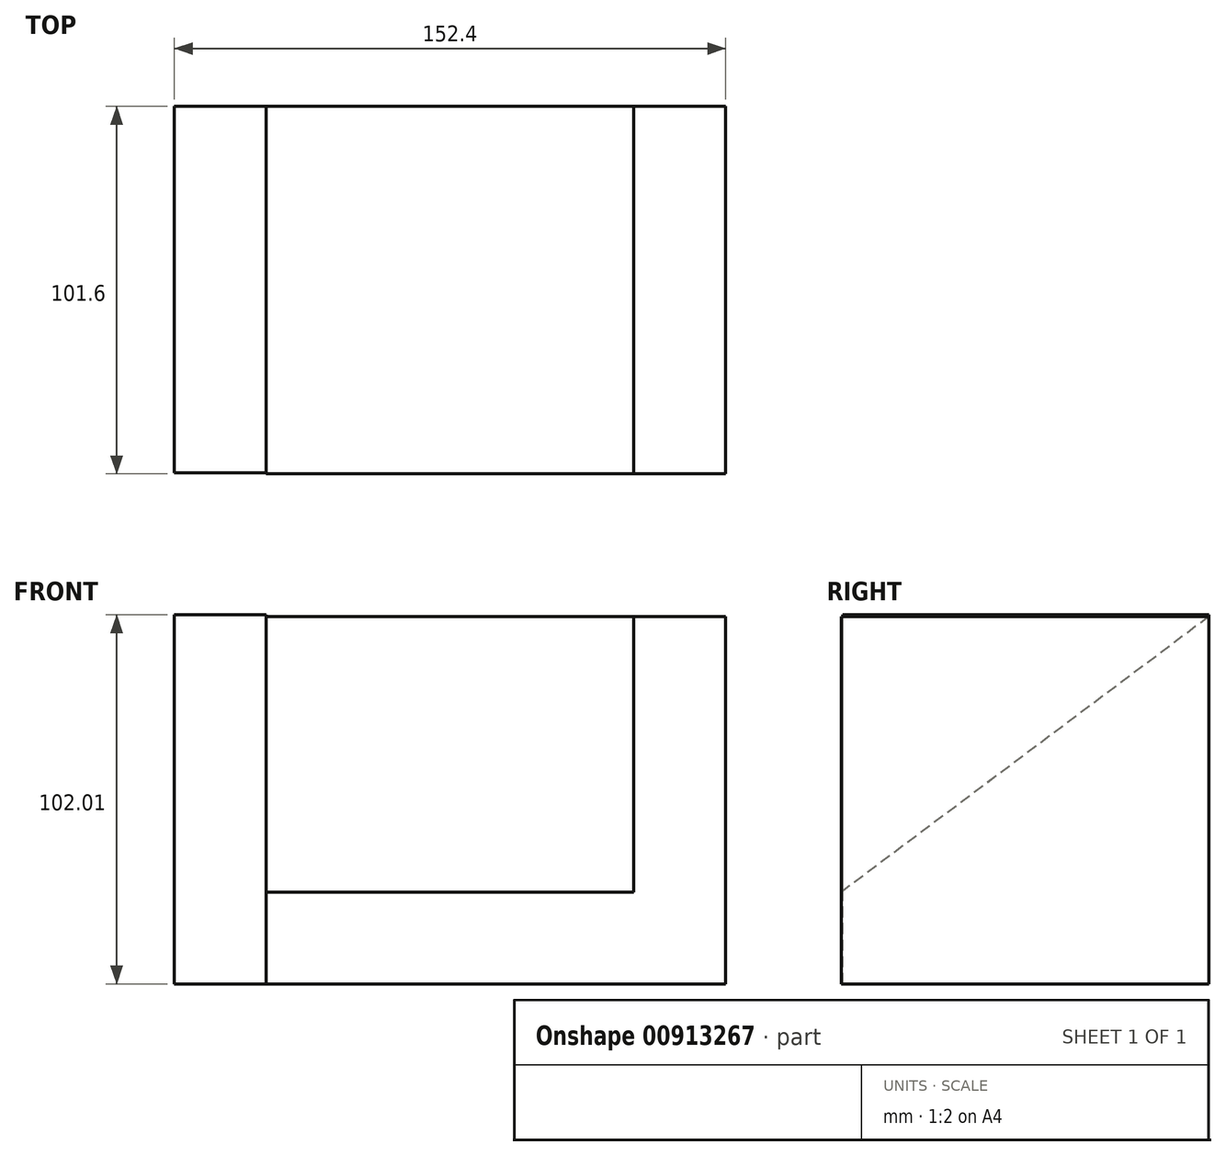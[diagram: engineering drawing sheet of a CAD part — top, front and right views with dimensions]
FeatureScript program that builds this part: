
annotation { "Feature Type Name" : "Feature", "Feature Type Description" : "" }
export const myFeature = defineFeature(function(context is Context, id is Id, definition is map)
    precondition{}
    {
        {
            var Q0;
            Q0=qCreatedBy(makeId("Top.planeOp"),FACE);
            var sketch = newSketch(context, id + "F0", { "sketchPlane" : qUnion([Q0])});
            skLineSegment(sketch, "E0.bottom", {"start": v(0, 0) * mm, "end": v(-101.6, 0) * mm});
            skLineSegment(sketch, "E0.top", {"start": v(0, -101.6) * mm, "end": v(-101.6, -101.6) * mm});
            skLineSegment(sketch, "E0.left", {"start": v(0, 0) * mm, "end": v(0, -101.6) * mm});
            skLineSegment(sketch, "E0.right", {"start": v(-101.6, 0) * mm, "end": v(-101.6, -101.6) * mm});
            skSolve(sketch);
        }
        {
            var Q0;
            Q0 = qSketchRegion(id + "F0", true);
            extrude(context, id + "F1", {"entities" : qUnion([Q0]), "depth" : 25.4 * mm, "offsetDistance" : 25.4 * mm});
        }
        {
            var Q0;
            Q0=makeQuery(id+"F1.opExtrude","SWEPT_FACE",FACE,{"disambiguationData":[OSD([sQuery(id+"F0.wireOp",EDGE,"E0.left")])]});
            var sketch = newSketch(context, id + "F2", { "sketchPlane" : qUnion([Q0])});
            skLineSegment(sketch, "E1.bottom", {"start": v(0, 25.4) * mm, "end": v(-101.6, 25.4) * mm});
            skLineSegment(sketch, "E1.top", {"start": v(0, 101.6) * mm, "end": v(-101.6, 101.6) * mm});
            skLineSegment(sketch, "E1.left", {"start": v(0, 25.4) * mm, "end": v(0, 101.6) * mm});
            skLineSegment(sketch, "E1.right", {"start": v(-101.6, 25.4) * mm, "end": v(-101.6, 101.6) * mm});
            skLineSegment(sketch, "E2", {"start": v(0, 101.6) * mm, "end": v(-101.6, 25.4) * mm});
            skSolve(sketch);
        }
        {
            var Q0;
            Q0=makeQuery(id+"F2.imprint","IMPRINT",FACE,{"disambiguationData":[TD([[makeQuery(id+"F2.imprint","IMPRINT",EDGE,{"derivedFrom":sQuery(id+"F2.wireOp",EDGE,"E1.bottom")}),-1.0]])]});
            extrude(context, id + "F3", {"entities" : qUnion([Q0]), "operationType" : NewBodyOperationType.ADD, "oppositeDirection" : true, "depth" : 101.6 * mm, "offsetDistance" : 25.4 * mm});
        }
        {
            var Q0;
            Q0=makeQuery(id+"F3.boolean.opBoolean","MERGE",FACE,{"derivedFrom":[makeQuery(id+"F1.opExtrude","SWEPT_FACE",FACE,{"disambiguationData":[OSD([sQuery(id+"F0.wireOp",EDGE,"E0.left")])]}),makeQuery(id+"F3.opExtrude","CAP_FACE",FACE,{"disambiguationData":[OSD([sQuery(id+"F2.wireOp",EDGE,"E1.bottom"),sQuery(id+"F2.wireOp",EDGE,"E1.left"),sQuery(id+"F2.wireOp",EDGE,"E2")])],"isStart":true})]});
            var sketch = newSketch(context, id + "F4", { "sketchPlane" : qUnion([Q0])});
            skLineSegment(sketch, "E3.bottom", {"start": v(-101.6, 0) * mm, "end": v(0, 0) * mm});
            skLineSegment(sketch, "E3.top", {"start": v(-101.6, 101.6) * mm, "end": v(0, 101.6) * mm});
            skLineSegment(sketch, "E3.left", {"start": v(-101.6, 0) * mm, "end": v(-101.6, 101.6) * mm});
            skLineSegment(sketch, "E3.right", {"start": v(0, 0) * mm, "end": v(0, 101.6) * mm});
            skSolve(sketch);
        }
        {
            var Q0;
            Q0 = qSketchRegion(id + "F4", true);
            extrude(context, id + "F5", {"entities" : qUnion([Q0]), "operationType" : NewBodyOperationType.ADD, "depth" : 25.4 * mm, "offsetDistance" : 25.4 * mm});
        }
        {
            var Q0;
            Q0=makeQuery(id+"F3.boolean.opBoolean","MERGE",FACE,{"derivedFrom":[makeQuery(id+"F1.opExtrude","SWEPT_FACE",FACE,{"disambiguationData":[OSD([sQuery(id+"F0.wireOp",EDGE,"E0.right")])]}),makeQuery(id+"F3.opExtrude","CAP_FACE",FACE,{"disambiguationData":[OSD([sQuery(id+"F2.wireOp",EDGE,"E1.bottom"),sQuery(id+"F2.wireOp",EDGE,"E1.left"),sQuery(id+"F2.wireOp",EDGE,"E2")])],"isStart":false})]});
            var sketch = newSketch(context, id + "F6", { "sketchPlane" : qUnion([Q0])});
            skLineSegment(sketch, "E4.bottom", {"start": v(0, 0) * mm, "end": v(101.3, 0) * mm});
            skLineSegment(sketch, "E4.top", {"start": v(0, 102) * mm, "end": v(101.3, 102) * mm});
            skLineSegment(sketch, "E4.left", {"start": v(0, 0) * mm, "end": v(0, 102) * mm});
            skLineSegment(sketch, "E4.right", {"start": v(101.3, 0) * mm, "end": v(101.3, 102) * mm});
            skSolve(sketch);
        }
        {
            var Q0;
            Q0 = qSketchRegion(id + "F6", true);
            extrude(context, id + "F7", {"entities" : qUnion([Q0]), "operationType" : NewBodyOperationType.ADD, "depth" : 25.4 * mm, "offsetDistance" : 25.4 * mm});
        }
    });
